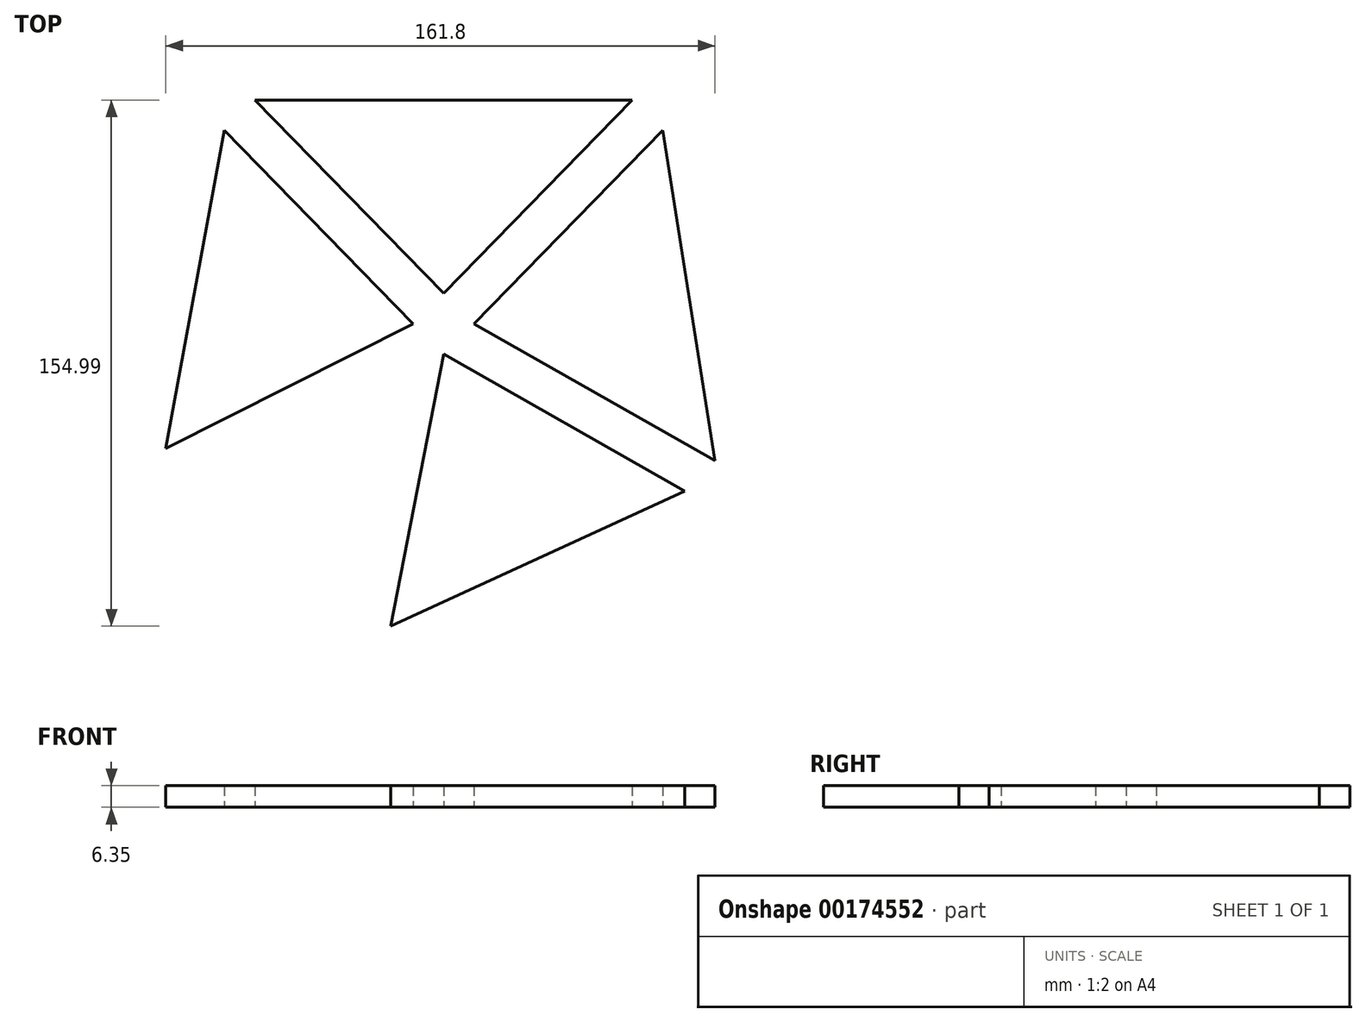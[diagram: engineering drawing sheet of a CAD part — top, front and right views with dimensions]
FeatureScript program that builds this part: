
annotation { "Feature Type Name" : "Feature", "Feature Type Description" : "" }
export const myFeature = defineFeature(function(context is Context, id is Id, definition is map)
    precondition{}
    {
        {
            var Q0;
            Q0=qCreatedBy(makeId("Top.planeOp"),FACE);
            var sketch = newSketch(context, id + "F0", { "sketchPlane" : qUnion([Q0])});
            skLineSegment(sketch, "E0", {"start": v(-55.58, 56.92) * mm, "end": v(0, 0) * mm});
            skLineSegment(sketch, "E1", {"start": v(0, 0) * mm, "end": v(-72.87, -36.75) * mm});
            skLineSegment(sketch, "E2", {"start": v(-72.87, -36.75) * mm, "end": v(-55.58, 56.92) * mm});
            skLineSegment(sketch, "E3", {"start": v(-46.6, 65.9) * mm, "end": v(8.98, 8.98) * mm});
            skLineSegment(sketch, "E4", {"start": v(8.98, 8.98) * mm, "end": v(64.56, 65.9) * mm});
            skLineSegment(sketch, "E5", {"start": v(64.56, 65.9) * mm, "end": v(-46.6, 65.9) * mm});
            skLineSegment(sketch, "E6", {"start": v(73.54, 56.92) * mm, "end": v(17.96, 0) * mm});
            skLineSegment(sketch, "E7", {"start": v(17.96, 0) * mm, "end": v(88.93, -40.3) * mm});
            skLineSegment(sketch, "E8", {"start": v(88.93, -40.3) * mm, "end": v(73.54, 56.92) * mm});
            skLineSegment(sketch, "E9", {"start": v(8.98, -8.98) * mm, "end": v(79.95, -49.27) * mm});
            skLineSegment(sketch, "E10", {"start": v(79.95, -49.27) * mm, "end": v(-6.58, -89.1) * mm});
            skLineSegment(sketch, "E11", {"start": v(-6.58, -89.1) * mm, "end": v(8.98, -8.98) * mm});
            skLineSegment(sketch, "E12", {"start": v(8.98, 8.98) * mm, "end": v(0, 0) * mm, "construction": true});
            skLineSegment(sketch, "E13", {"start": v(8.98, -8.98) * mm, "end": v(0, 0) * mm, "construction": true});
            skLineSegment(sketch, "E14", {"start": v(8.98, 8.98) * mm, "end": v(17.96, 0) * mm, "construction": true});
            skLineSegment(sketch, "E15", {"start": v(17.96, 0) * mm, "end": v(8.98, -8.98) * mm, "construction": true});
            skSolve(sketch);
        }
        {
            var Q0;
            Q0=qCreatedBy(makeId("Top.planeOp"),FACE);
            var sketch = newSketch(context, id + "F1", { "sketchPlane" : qUnion([Q0])});
            skLineSegment(sketch, "E16.0.0", {"start": v(0, 0) * mm, "end": v(-55.58, 56.92) * mm});
            skLineSegment(sketch, "E16.0.1", {"start": v(-55.58, 56.92) * mm, "end": v(-72.87, -36.75) * mm});
            skLineSegment(sketch, "E16.0.2", {"start": v(-72.87, -36.75) * mm, "end": v(0, 0) * mm});
            skLineSegment(sketch, "E17.0.0", {"start": v(64.56, 65.9) * mm, "end": v(-46.6, 65.9) * mm});
            skLineSegment(sketch, "E17.0.1", {"start": v(-46.6, 65.9) * mm, "end": v(8.98, 8.98) * mm});
            skLineSegment(sketch, "E17.0.2", {"start": v(8.98, 8.98) * mm, "end": v(64.56, 65.9) * mm});
            skLineSegment(sketch, "E18.0.0", {"start": v(88.93, -40.3) * mm, "end": v(73.54, 56.92) * mm});
            skLineSegment(sketch, "E18.0.1", {"start": v(73.54, 56.92) * mm, "end": v(17.96, 0) * mm});
            skLineSegment(sketch, "E18.0.2", {"start": v(17.96, 0) * mm, "end": v(88.93, -40.3) * mm});
            skLineSegment(sketch, "E19.0.0", {"start": v(79.95, -49.27) * mm, "end": v(8.98, -8.98) * mm});
            skLineSegment(sketch, "E19.0.1", {"start": v(8.98, -8.98) * mm, "end": v(-6.58, -89.1) * mm});
            skLineSegment(sketch, "E19.0.2", {"start": v(-6.58, -89.1) * mm, "end": v(79.95, -49.27) * mm});
            skSolve(sketch);
        }
        {
            var Q0;
            Q0 = qSketchRegion(id + "F1", true);
            extrude(context, id + "F2", {"entities" : qUnion([Q0]), "depth" : 6.35 * mm});
        }
    });
